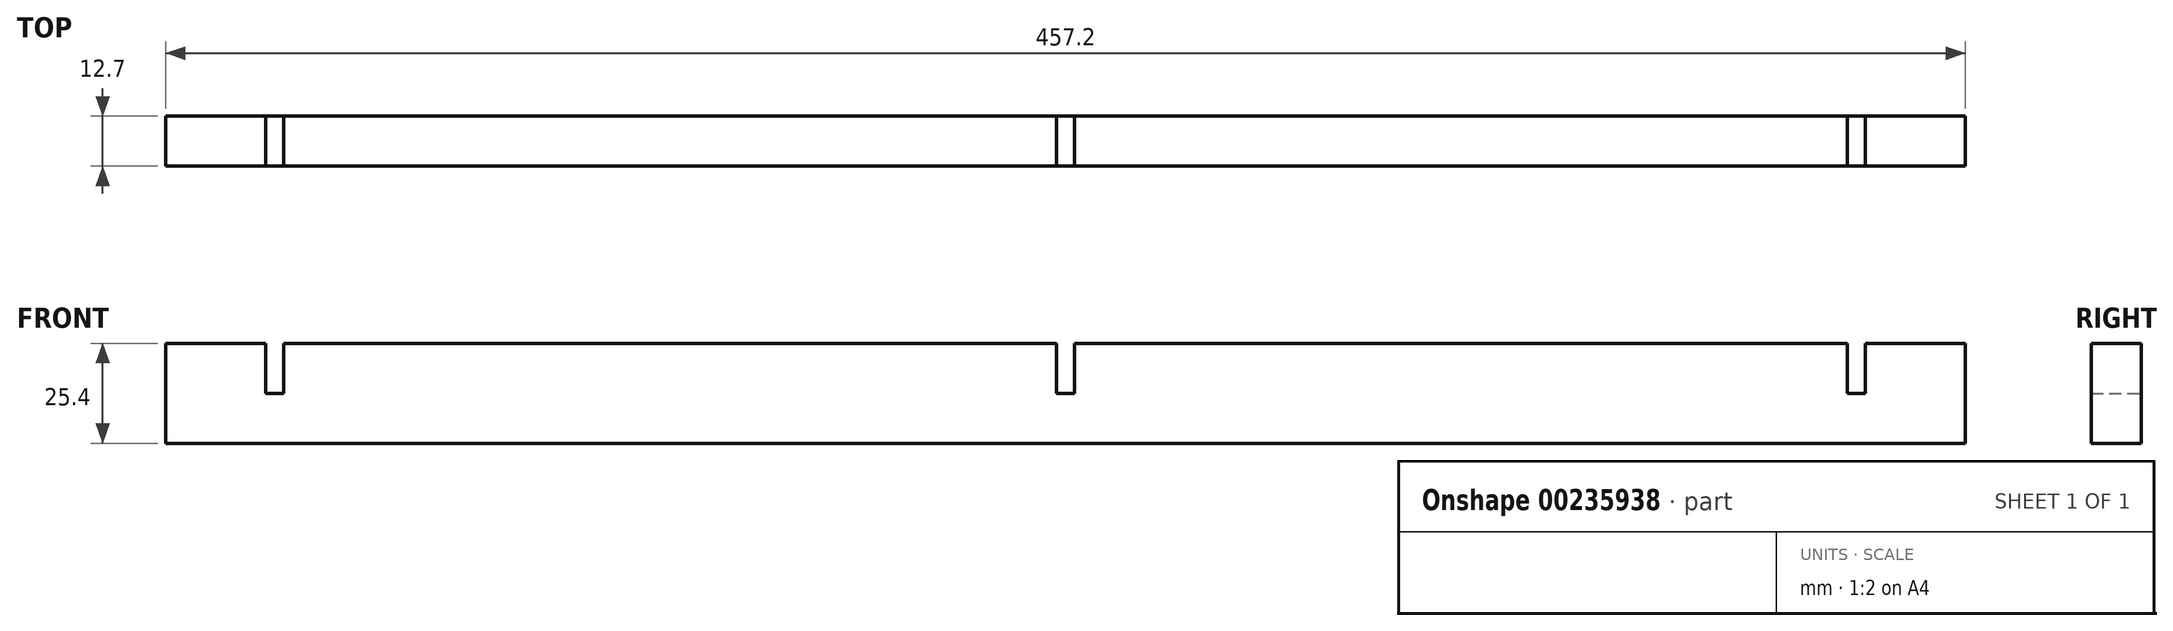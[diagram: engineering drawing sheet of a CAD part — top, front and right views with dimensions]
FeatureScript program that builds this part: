
annotation { "Feature Type Name" : "Feature", "Feature Type Description" : "" }
export const myFeature = defineFeature(function(context is Context, id is Id, definition is map)
    precondition{}
    {
        {
            var Q0;
            Q0=qCreatedBy(makeId("Front.planeOp"),FACE);
            var sketch = newSketch(context, id + "F0", { "sketchPlane" : qUnion([Q0])});
            skLineSegment(sketch, "E0", {"start": v(-191, -23.76) * mm, "end": v(266.2, -23.76) * mm});
            skLineSegment(sketch, "E1", {"start": v(266.2, -23.76) * mm, "end": v(266.2, 1.64) * mm});
            skLineSegment(sketch, "E2", {"start": v(266.2, 1.64) * mm, "end": v(240.8, 1.64) * mm});
            skLineSegment(sketch, "E3", {"start": v(240.8, 1.64) * mm, "end": v(240.8, -11.06) * mm});
            skLineSegment(sketch, "E4", {"start": v(240.8, -11.06) * mm, "end": v(236.19, -11.06) * mm});
            skLineSegment(sketch, "E5", {"start": v(236.19, -11.06) * mm, "end": v(236.19, 1.64) * mm});
            skLineSegment(sketch, "E6", {"start": v(236.19, 1.64) * mm, "end": v(-160.97, 1.64) * mm});
            skLineSegment(sketch, "E7", {"start": v(-160.97, 1.64) * mm, "end": v(-160.97, -11.06) * mm});
            skLineSegment(sketch, "E8", {"start": v(-160.97, -11.06) * mm, "end": v(-165.6, -11.06) * mm});
            skLineSegment(sketch, "E9", {"start": v(-165.6, -11.06) * mm, "end": v(-165.6, 1.64) * mm});
            skLineSegment(sketch, "E10", {"start": v(-165.6, 1.64) * mm, "end": v(-191, 1.64) * mm});
            skLineSegment(sketch, "E11", {"start": v(-191, 1.64) * mm, "end": v(-191, -23.76) * mm});
            skSolve(sketch);
        }
        {
            var Q0;
            Q0 = qSketchRegion(id + "F0", true);
            extrude(context, id + "F1", {"entities" : qUnion([Q0]), "depth" : 12.7 * mm});
        }
        {
            var Q0;
            Q0=makeQuery(id+"F1.opExtrude","CAP_FACE",FACE,{"disambiguationData":[OSD([sQuery(id+"F0.wireOp",EDGE,"E0"),sQuery(id+"F0.wireOp",EDGE,"E1"),sQuery(id+"F0.wireOp",EDGE,"E2"),sQuery(id+"F0.wireOp",EDGE,"E3"),sQuery(id+"F0.wireOp",EDGE,"E4"),sQuery(id+"F0.wireOp",EDGE,"E5"),sQuery(id+"F0.wireOp",EDGE,"E6"),sQuery(id+"F0.wireOp",EDGE,"E7"),sQuery(id+"F0.wireOp",EDGE,"E8"),sQuery(id+"F0.wireOp",EDGE,"E9"),sQuery(id+"F0.wireOp",EDGE,"E10"),sQuery(id+"F0.wireOp",EDGE,"E11")])],"isStart":false});
            var sketch = newSketch(context, id + "F2", { "sketchPlane" : qUnion([Q0])});
            skPoint(sketch, "E12", {"position": v(37.6, 1.64) * mm});
            skLineSegment(sketch, "E13.bottom", {"start": v(35.3, 1.64) * mm, "end": v(39.92, 1.64) * mm});
            skLineSegment(sketch, "E13.top", {"start": v(35.3, -11.06) * mm, "end": v(39.92, -11.06) * mm});
            skLineSegment(sketch, "E13.left", {"start": v(35.3, 1.64) * mm, "end": v(35.3, -11.06) * mm});
            skLineSegment(sketch, "E13.right", {"start": v(39.92, 1.64) * mm, "end": v(39.92, -11.06) * mm});
            skPoint(sketch, "E13.middle", {"position": v(37.6, -4.71) * mm});
            skSolve(sketch);
        }
        {
            var Q0;
            Q0=makeQuery(id+"F2.imprint","IMPRINT",FACE,{"disambiguationData":[TD([[makeQuery(id+"F2.imprint","IMPRINT",EDGE,{"derivedFrom":sQuery(id+"F2.wireOp",EDGE,"E13.bottom")}),1.0]])]});
            extrude(context, id + "F3", {"entities" : qUnion([Q0]), "operationType" : NewBodyOperationType.REMOVE, "oppositeDirection" : true, "depth" : 25.4 * mm});
        }
    });
